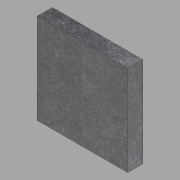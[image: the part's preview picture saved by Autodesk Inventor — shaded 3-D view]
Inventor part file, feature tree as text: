
AUTODESK INVENTOR PART (.ipt)
format: ipt  version: 2022.1 (Build 261234020, 234B)  size: 101,376 bytes
history: native  units: in
note: dims shown in document units (in); Inventor stores cm internally (conversion verified against a paired STEP export)
features: extrude x1, sketch x1
ambient origin geometry x8: Origin, YZ Plane, XZ Plane, XY Plane, X Axis, Y Axis, Z Axis, Center Point
bodies: Solid1 (feature_tree)
feature tree (2):
  extrude  "Extrusion1"  Depth=36.0in
  sketch  "Sketch1"  dims[d0=36.0in d1=36.0in d2=6.0in d3=0.0in]
